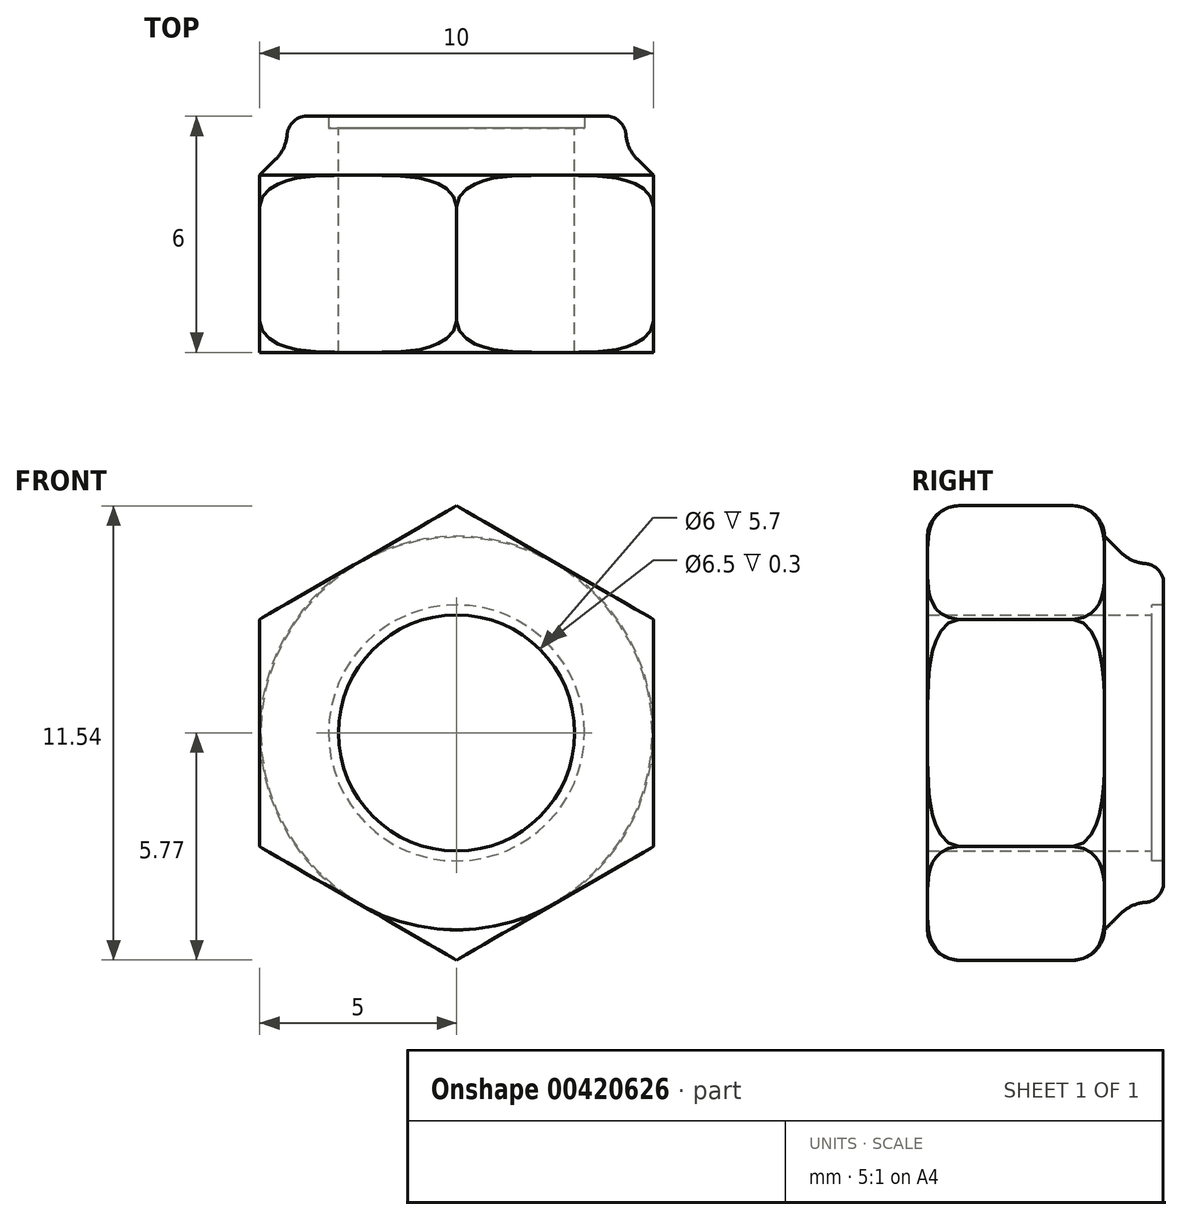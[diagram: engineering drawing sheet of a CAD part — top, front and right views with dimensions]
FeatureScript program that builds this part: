
annotation { "Feature Type Name" : "Feature", "Feature Type Description" : "" }
export const myFeature = defineFeature(function(context is Context, id is Id, definition is map)
    precondition{}
    {
        {
            var Q0;
            Q0=qCreatedBy(makeId("Front.planeOp"),FACE);
            var sketch = newSketch(context, id + "F0", { "sketchPlane" : qUnion([Q0])});
            skCircle(sketch, "E0", {"center": v(0, 0) * mm, "radius": 5.77 * mm});
            skCircle(sketch, "E1", {"center": v(0, 0) * mm, "radius": 3 * mm});
            skCircle(sketch, "E2.cCircle", {"center": v(0, 0) * mm, "radius": 5 * mm, "construction": true});
            skLineSegment(sketch, "E2.0", {"start": v(-5.77, 0) * mm, "end": v(-2.89, 5) * mm, "construction": true});
            skLineSegment(sketch, "E2.1", {"start": v(-2.89, 5) * mm, "end": v(2.89, 5) * mm, "construction": true});
            skLineSegment(sketch, "E2.2", {"start": v(2.89, 5) * mm, "end": v(5.77, 0) * mm, "construction": true});
            skLineSegment(sketch, "E2.3", {"start": v(5.77, 0) * mm, "end": v(2.89, -5) * mm, "construction": true});
            skLineSegment(sketch, "E2.4", {"start": v(2.89, -5) * mm, "end": v(-2.89, -5) * mm, "construction": true});
            skLineSegment(sketch, "E2.5", {"start": v(-2.89, -5) * mm, "end": v(-5.77, 0) * mm, "construction": true});
            skPoint(sketch, "E2.0.midPoint", {"position": v(-4.33, 2.5) * mm});
            skSolve(sketch);
        }
        {
            var Q0;
            Q0 = qSketchRegion(id + "F0", true);
            extrude(context, id + "F1", {"entities" : qUnion([Q0]), "depth" : 4.5 * mm, "symmetric" : true});
        }
        {
            var Q0;
            Q0=makeQuery(id+"F1.opExtrude","CAP_FACE",FACE,{"disambiguationData":[OSD([sQuery(id+"F0.wireOp",EDGE,"E0"),sQuery(id+"F0.wireOp",EDGE,"E1")])],"isStart":false});
            var sketch = newSketch(context, id + "F2", { "sketchPlane" : qUnion([Q0])});
            skCircle(sketch, "E3.cCircle", {"center": v(0, 0) * mm, "radius": 5 * mm, "construction": true});
            skLineSegment(sketch, "E3.0", {"start": v(-5, -2.89) * mm, "end": v(-5, 2.89) * mm});
            skLineSegment(sketch, "E3.1", {"start": v(-5, 2.89) * mm, "end": v(0, 5.77) * mm});
            skLineSegment(sketch, "E3.2", {"start": v(0, 5.77) * mm, "end": v(5, 2.89) * mm});
            skLineSegment(sketch, "E3.3", {"start": v(5, 2.89) * mm, "end": v(5, -2.89) * mm});
            skLineSegment(sketch, "E3.4", {"start": v(5, -2.89) * mm, "end": v(0, -5.77) * mm});
            skLineSegment(sketch, "E3.5", {"start": v(0, -5.77) * mm, "end": v(-5, -2.89) * mm});
            skPoint(sketch, "E3.0.midPoint", {"position": v(-5, 0) * mm});
            skCircle(sketch, "E4", {"center": v(0, 0) * mm, "radius": 6 * mm});
            skSolve(sketch);
        }
        {
            var Q0;
            Q0=makeQuery(id+"F1.opExtrude","CAP_EDGE",EDGE,{"disambiguationData":[OSD([sQuery(id+"F0.wireOp",EDGE,"E0")])],"isStart":false});
            var Q1;
            Q1=makeQuery(id+"F1.opExtrude","CAP_EDGE",EDGE,{"disambiguationData":[OSD([sQuery(id+"F0.wireOp",EDGE,"E0")])],"isStart":true});
            fillet(context, id + "F3", {"entities" : qUnion([Q0, Q1]), "radius" : 0.8 * mm, "tangentPropagation" : true, "allowEdgeOverflow" : false});
        }
        {
            var Q0;
            Q0 = qSketchRegion(id + "F2", true);
            extrude(context, id + "F4", {"entities" : qUnion([Q0]), "operationType" : NewBodyOperationType.REMOVE, "endBound" : BoundingType.THROUGH_ALL, "oppositeDirection" : true, "depth" : 25 * mm});
        }
        {
            var Q0;
            Q0=qCreatedBy(makeId("Top.planeOp"),FACE);
            var sketch = newSketch(context, id + "F5", { "sketchPlane" : qUnion([Q0])});
            skLineSegment(sketch, "E5", {"start": v(-5, 2.25) * mm, "end": v(-4.3, 2.95) * mm});
            skLineSegment(sketch, "E6", {"start": v(-4.3, 2.95) * mm, "end": v(-4.3, 3.75) * mm});
            skLineSegment(sketch, "E7", {"start": v(-4.3, 3.75) * mm, "end": v(-3, 3.75) * mm, "construction": true});
            skLineSegment(sketch, "E8", {"start": v(-3, 3.75) * mm, "end": v(-3, 2.25) * mm, "construction": true});
            skLineSegment(sketch, "E9", {"start": v(-3, 2.25) * mm, "end": v(-5, 2.25) * mm});
            skLineSegment(sketch, "E10", {"start": v(0, 0) * mm, "end": v(0, 5.75) * mm, "construction": true});
            skLineSegment(sketch, "E11", {"start": v(-3, 2.25) * mm, "end": v(-3, 3.45) * mm});
            skLineSegment(sketch, "E12", {"start": v(-3, 3.45) * mm, "end": v(-3.25, 3.45) * mm});
            skLineSegment(sketch, "E13", {"start": v(-3.25, 3.45) * mm, "end": v(-3.25, 3.75) * mm});
            skLineSegment(sketch, "E14", {"start": v(-3.25, 3.75) * mm, "end": v(-4.3, 3.75) * mm});
            skSolve(sketch);
        }
        {
            var Q0;
            Q0 = qSketchRegion(id + "F5", true);
            var Q1;
            Q1=sQuery(id+"F5.wireOp",EDGE,"E10");
            revolve(context, id + "F6", {"operationType" : NewBodyOperationType.ADD, "entities" : qUnion([Q0]), "axis" : qUnion([Q1]), "revolveType" : RevolveType.FULL});
        }
        {
            var Q0;
            Q0=makeQuery(id+"F6.opRevolve","SWEPT_EDGE",EDGE,{"disambiguationData":[OSD([sQuery(id+"F5.wireOp",EDGE,"E5"),sQuery(id+"F5.wireOp",EDGE,"E6")])]});
            fillet(context, id + "F7", {"entities" : qUnion([Q0]), "radius" : 1 * mm, "tangentPropagation" : true, "allowEdgeOverflow" : false});
        }
        {
            var Q0;
            Q0=makeQuery(id+"F6.opRevolve","SWEPT_EDGE",EDGE,{"disambiguationData":[OSD([sQuery(id+"F5.wireOp",EDGE,"E6"),sQuery(id+"F5.wireOp",EDGE,"E7")])]});
            fillet(context, id + "F8", {"entities" : qUnion([Q0]), "radius" : 0.5 * mm, "tangentPropagation" : true, "allowEdgeOverflow" : false});
        }
    });
